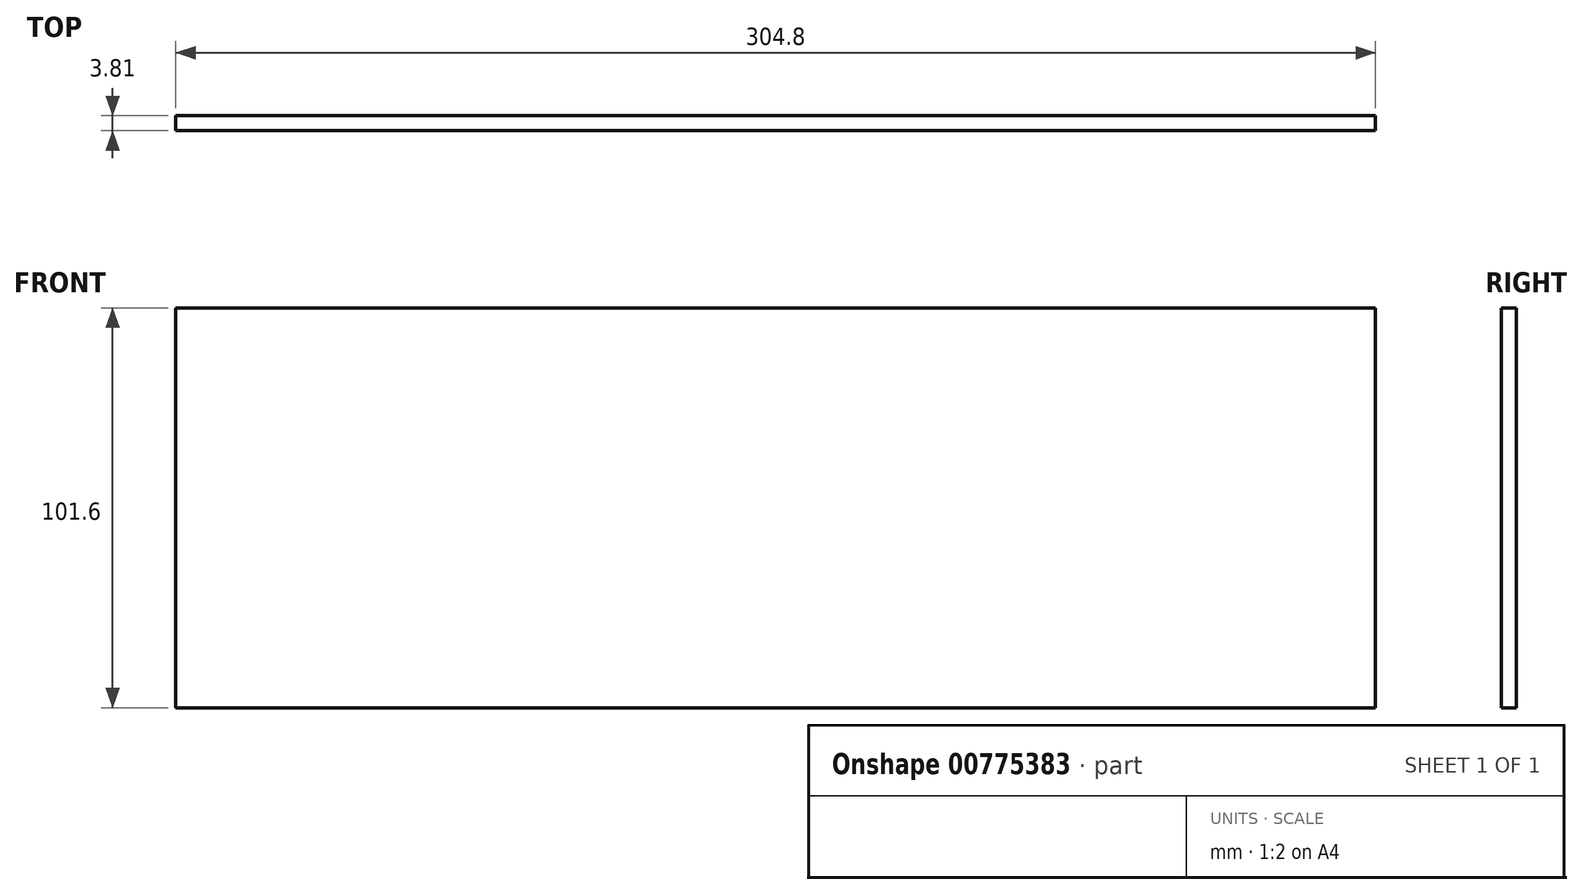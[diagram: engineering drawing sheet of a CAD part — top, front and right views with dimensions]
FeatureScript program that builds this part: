
annotation { "Feature Type Name" : "Feature", "Feature Type Description" : "" }
export const myFeature = defineFeature(function(context is Context, id is Id, definition is map)
    precondition{}
    {
        {
            var Q0;
            Q0=qCreatedBy(makeId("Front.planeOp"),FACE);
            var sketch = newSketch(context, id + "F0", { "sketchPlane" : qUnion([Q0])});
            skLineSegment(sketch, "E0.bottom", {"start": v(-152.4, 50.8) * mm, "end": v(152.4, 50.8) * mm});
            skLineSegment(sketch, "E0.top", {"start": v(-152.4, -50.8) * mm, "end": v(152.4, -50.8) * mm});
            skLineSegment(sketch, "E0.left", {"start": v(-152.4, 50.8) * mm, "end": v(-152.4, -50.8) * mm});
            skLineSegment(sketch, "E0.right", {"start": v(152.4, 50.8) * mm, "end": v(152.4, -50.8) * mm});
            skPoint(sketch, "E0.middle", {"position": v(0, 0) * mm});
            skSolve(sketch);
        }
        {
            var Q0;
            Q0 = qSketchRegion(id + "F0", true);
            extrude(context, id + "F1", {"entities" : qUnion([Q0]), "depth" : 3.8 * mm, "offsetDistance" : 25.4 * mm});
        }
    });
